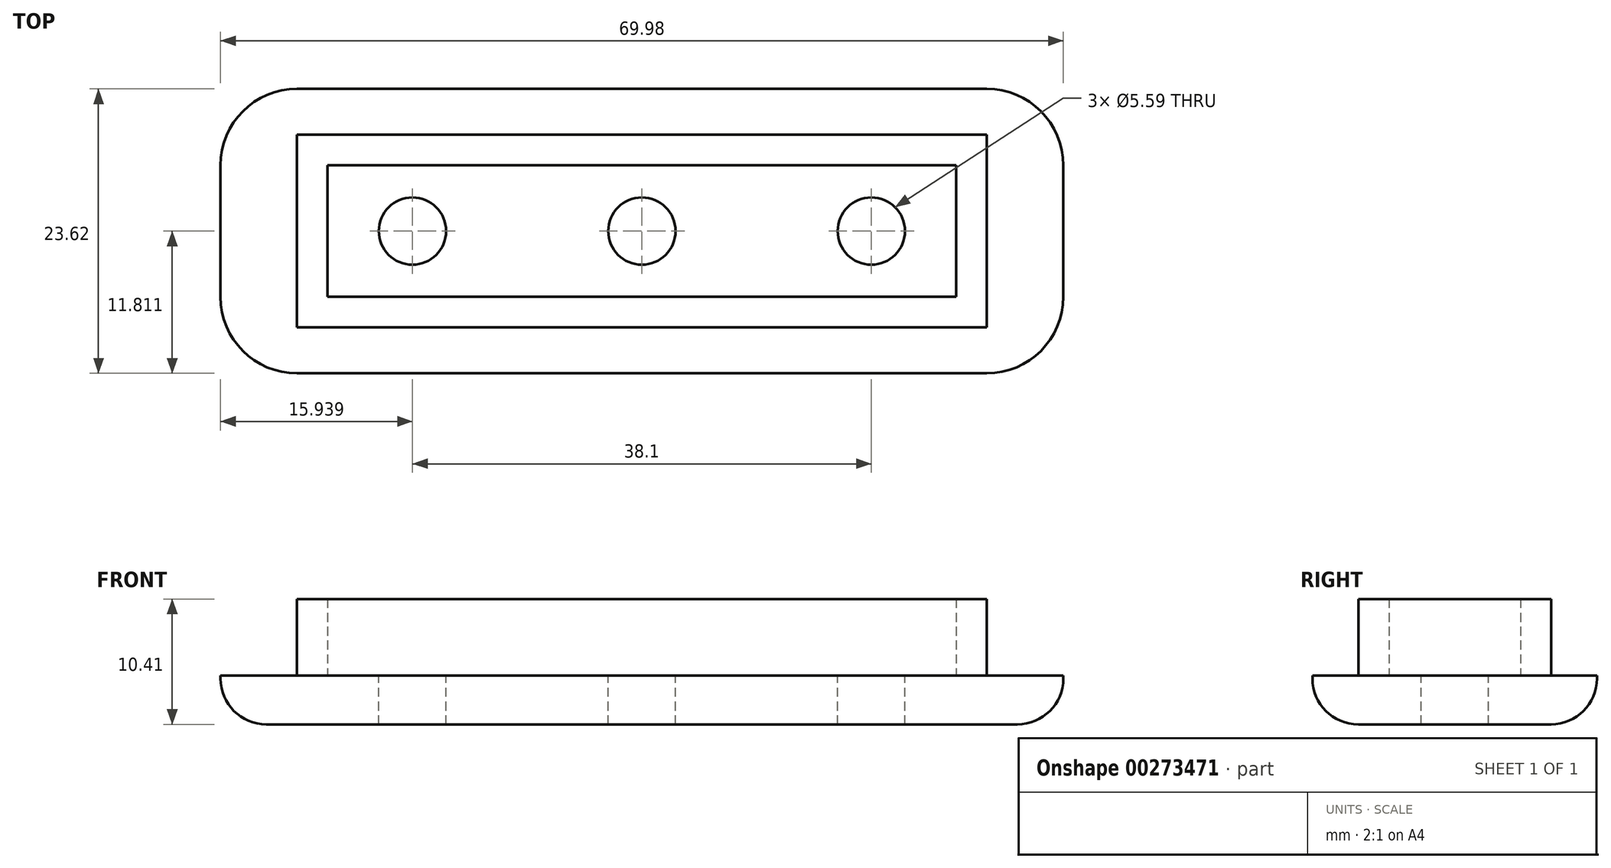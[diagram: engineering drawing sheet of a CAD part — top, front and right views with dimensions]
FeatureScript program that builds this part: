
annotation { "Feature Type Name" : "Feature", "Feature Type Description" : "" }
export const myFeature = defineFeature(function(context is Context, id is Id, definition is map)
    precondition{}
    {
        {
            var Q0;
            Q0=qCreatedBy(makeId("Top.planeOp"),FACE);
            var sketch = newSketch(context, id + "F0", { "sketchPlane" : qUnion([Q0])});
            skLineSegment(sketch, "E0.bottom", {"start": v(0, 0) * mm, "end": v(52.2, 0) * mm});
            skLineSegment(sketch, "E0.top", {"start": v(0, 10.92) * mm, "end": v(52.2, 10.92) * mm});
            skLineSegment(sketch, "E0.left", {"start": v(0, 0) * mm, "end": v(0, 10.92) * mm});
            skLineSegment(sketch, "E0.right", {"start": v(52.2, 0) * mm, "end": v(52.2, 10.92) * mm});
            skLineSegment(sketch, "E1.bottom", {"start": v(-2.54, 17.27) * mm, "end": v(54.74, 17.27) * mm});
            skLineSegment(sketch, "E1.top", {"start": v(-2.54, -6.35) * mm, "end": v(54.74, -6.35) * mm});
            skLineSegment(sketch, "E1.left", {"start": v(-8.9, 10.92) * mm, "end": v(-8.9, 0) * mm});
            skLineSegment(sketch, "E1.right", {"start": v(61.09, 10.92) * mm, "end": v(61.09, 0) * mm});
            skPoint(sketch, "E1.middle", {"position": v(26.1, 5.46) * mm});
            skPoint(sketch, "E1.middle.positionSnap0", {"position": v(0, 5.46) * mm});
            skPoint(sketch, "E1.middle.positionSnap1", {"position": v(26.1, 10.92) * mm});
            skPoint(sketch, "E1.centerSnap0", {"position": v(0, 5.46) * mm});
            skPoint(sketch, "E1.centerSnap1", {"position": v(26.1, 10.92) * mm});
            skCircle(sketch, "E2", {"center": v(26.1, 5.46) * mm, "radius": 2.8 * mm});
            skCircle(sketch, "E3", {"center": v(45.15, 5.46) * mm, "radius": 2.8 * mm});
            skCircle(sketch, "E4", {"center": v(7.05, 5.46) * mm, "radius": 2.8 * mm});
            skPoint(sketch, "E5.visualSharp", {"position": v(-8.9, 17.27) * mm});
            skArc(sketch, "E5.filletArc", {"start": v(-2.54, 17.27) * mm, "mid": v(-7.03, 15.41) * mm, "end": v(-8.9, 10.92) * mm});
            skPoint(sketch, "E6.visualSharp", {"position": v(-8.9, -6.35) * mm});
            skArc(sketch, "E6.filletArc", {"start": v(-8.9, 0) * mm, "mid": v(-7.03, -4.5) * mm, "end": v(-2.54, -6.35) * mm});
            skPoint(sketch, "E7.visualSharp", {"position": v(61.09, 17.27) * mm});
            skArc(sketch, "E7.filletArc", {"start": v(61.09, 10.92) * mm, "mid": v(59.23, 15.41) * mm, "end": v(54.74, 17.27) * mm});
            skPoint(sketch, "E8.visualSharp", {"position": v(61.09, -6.35) * mm});
            skArc(sketch, "E8.filletArc", {"start": v(54.74, -6.35) * mm, "mid": v(59.23, -4.5) * mm, "end": v(61.09, 0) * mm});
            skLineSegment(sketch, "E9.0", {"start": v(-2.54, -2.54) * mm, "end": v(-2.54, 13.46) * mm});
            skLineSegment(sketch, "E9.1", {"start": v(-2.54, -2.54) * mm, "end": v(54.74, -2.54) * mm});
            skLineSegment(sketch, "E9.2", {"start": v(54.74, -2.54) * mm, "end": v(54.74, 13.46) * mm});
            skLineSegment(sketch, "E9.3", {"start": v(-2.54, 13.46) * mm, "end": v(54.74, 13.46) * mm});
            skSolve(sketch);
        }
        {
            var Q0;
            Q0 = qSketchRegion(id + "F0", true);
            var Q1;
            Q1=makeQuery(id+"F0.imprint","IMPRINT",FACE,{"disambiguationData":[TD([[makeQuery(id+"F0.imprint","IMPRINT",EDGE,{"derivedFrom":sQuery(id+"F0.wireOp",EDGE,"E0.bottom")}),-1.0]])]});
            var Q2;
            Q2=makeQuery(id+"F0.imprint","IMPRINT",FACE,{"disambiguationData":[TD([[makeQuery(id+"F0.imprint","IMPRINT",EDGE,{"derivedFrom":sQuery(id+"F0.wireOp",EDGE,"E0.bottom")}),1.0]])]});
            extrude(context, id + "F1", {"entities" : qUnion([Q0, Q1, Q2]), "oppositeDirection" : true, "depth" : 4.06 * mm});
        }
        {
            var Q0;
            Q0=makeQuery(id+"F0.imprint","IMPRINT",FACE,{"disambiguationData":[TD([[makeQuery(id+"F0.imprint","IMPRINT",EDGE,{"derivedFrom":sQuery(id+"F0.wireOp",EDGE,"E0.bottom")}),-1.0]])]});
            extrude(context, id + "F2", {"entities" : qUnion([Q0]), "operationType" : NewBodyOperationType.ADD, "depth" : 6.35 * mm});
        }
        {
            var Q0;
            Q0=makeQuery(id+"F1.opExtrude","CAP_EDGE",EDGE,{"disambiguationData":[OSD([sQuery(id+"F0.wireOp",EDGE,"E1.top")])],"isStart":false});
            fillet(context, id + "F3", {"entities" : qUnion([Q0]), "radius" : 3.8 * mm, "tangentPropagation" : true, "allowEdgeOverflow" : false});
        }
    });
